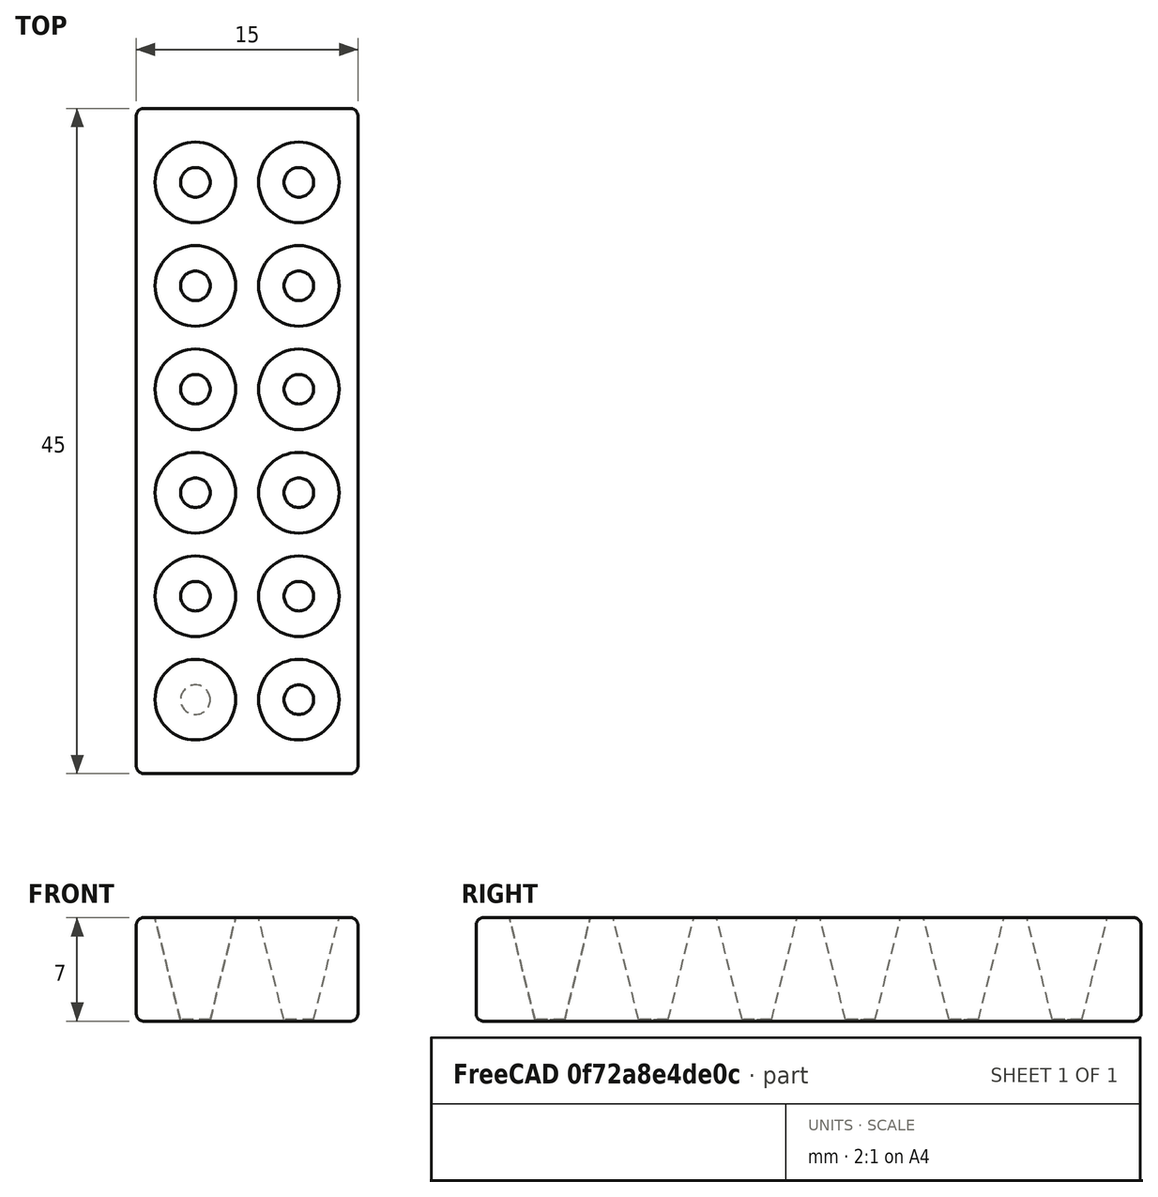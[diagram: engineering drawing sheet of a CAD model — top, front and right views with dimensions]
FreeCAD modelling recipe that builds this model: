
FCSTD DOCUMENT  (FreeCAD 0.21R33694 (Git))
Label: prodriguez_repte2
License: All rights reserved
LicenseURL: https://en.wikipedia.org/wiki/All_rights_reserved
objects: Part::Box×1, Part::Cone×1, Part::FeaturePython×1, Part::Fillet×1, Part::Cut×1
note: 4 computed .brp shape members not serialized (recipe doc carries the construction recipe); baked Part::Feature solids carry a one-line shape summary decoded from their .brp

FEATURE [Part::Box] Box  label="Cub"
  AttacherType = Attacher::AttachEngine3D
  Height = 7
  Length = 15
  Placement = pos=(-0.5,0,0) rot=(0,0,1;0rad)
  Width = 45
  expr: .Placement.Base.x = -0.5
FEATURE [Part::Cone] Cone  label="Con"
  Angle = 360
  AttacherType = Attacher::AttachEngine3D
  Height = 6.99
  Placement = pos=(3.5,5,0) rot=(0,0,1;0rad)
  Radius1 = 1
  Radius2 = 2.75
  expr: .Placement.Base.x = 3.5
FEATURE [Part::FeaturePython] Array  # Draft array (typed FeaturePython)
  AlwaysSyncPlacement = false
  Angle = 360
  ArrayType = 0
  Axis = (0,0,1)
  Base = -> Cone
  Center = (0,0,0)
  Count = 12
  ExpandArray = false
  Fuse = false
  IntervalAxis = (0,0,0)
  IntervalX = (7,0,0)
  IntervalY = (0,7,0)
  IntervalZ = (0,0,100)
  NumberCircles = 3
  NumberPolar = 5
  NumberX = 2
  NumberY = 6
  NumberZ = 1
  Placement = pos=(0,0,0.1) rot=(0,0,1;0rad)
  PlacementList = 12 placements: [(3.5,5,0),(3.5,12,0),(3.5,19,0),(3.5,26,0),(3.5,33,0),(3.5,40,0),(10.5,5,0),(10.5,12,0),(10.5,19,0),(10.5,26,0),(10.5,33,0),(10.5,40,0)]
  RadialDistance = 50
  ScaleList = (12) [(1,1,1),(1,1,1),(1,1,1),(1,1,1),(1,1,1),(1,1,1),(1,1,1),(1,1,1),(1,1,1),(1,1,1),(1,1,1),(1,1,1)]
  Symmetry = 1
  TangentialDistance = 25
  expr: .Placement.Base.z = 0.1
FEATURE [Part::Fillet] Fillet
  Base = -> Box
  Edges = 12 edges r=0.5: [Edge1,Edge2,Edge3,Edge4,Edge5,Edge6,Edge7,Edge8,Edge9,Edge10,Edge11,Edge12]
FEATURE [Part::Cut] Cut
  Base = -> Fillet
  Tool = -> Array
